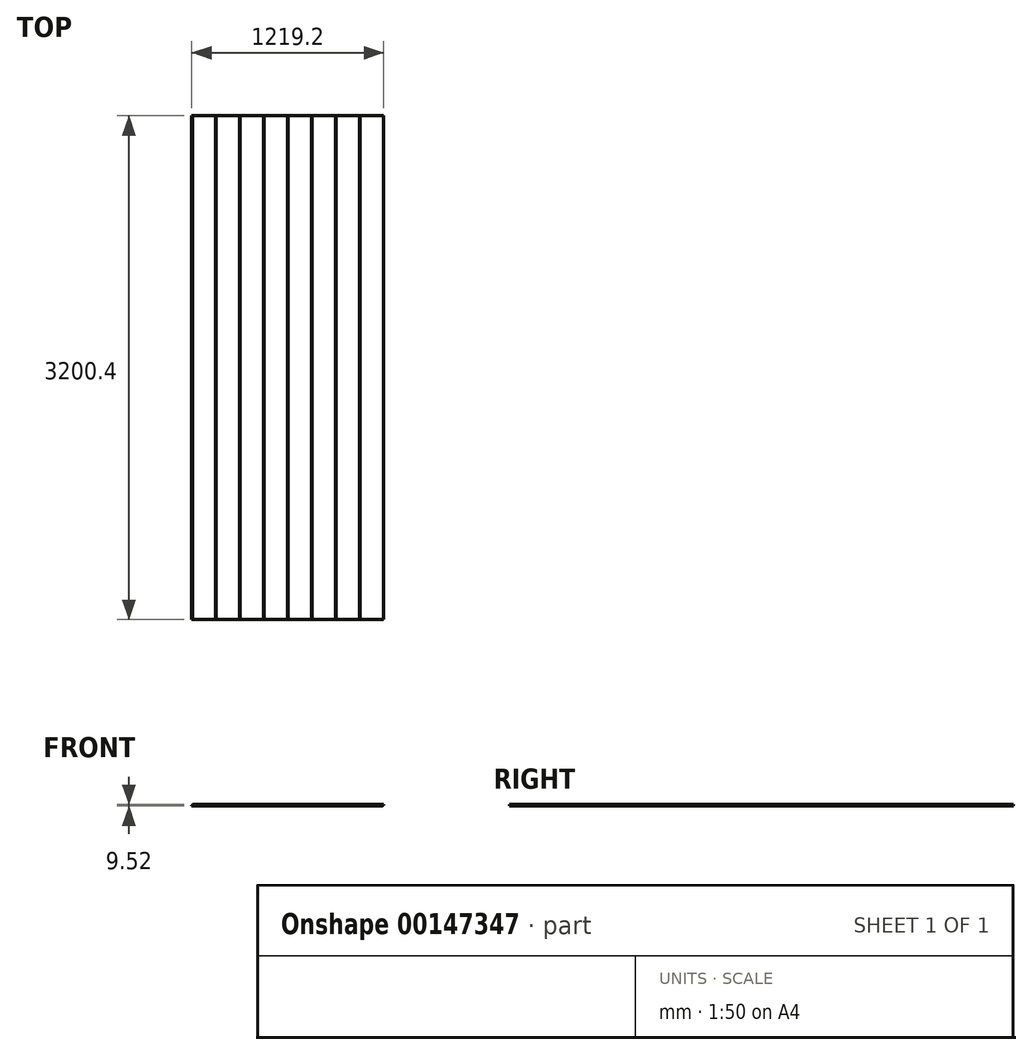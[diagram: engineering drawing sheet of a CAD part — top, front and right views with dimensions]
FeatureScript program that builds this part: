
annotation { "Feature Type Name" : "Feature", "Feature Type Description" : "" }
export const myFeature = defineFeature(function(context is Context, id is Id, definition is map)
    precondition{}
    {
        {
            var Q0;
            Q0=qCreatedBy(makeId("Top.planeOp"),FACE);
            var sketch = newSketch(context, id + "F0", { "sketchPlane" : qUnion([Q0])});
            skLineSegment(sketch, "E0.bottom", {"start": v(-609.6, 3130.65) * mm, "end": v(609.6, 3130.65) * mm});
            skLineSegment(sketch, "E0.top", {"start": v(-609.6, -523.78) * mm, "end": v(609.6, -523.78) * mm});
            skLineSegment(sketch, "E0.left", {"start": v(-609.6, 3130.65) * mm, "end": v(-609.6, -523.78) * mm});
            skLineSegment(sketch, "E0.right", {"start": v(609.6, 3130.65) * mm, "end": v(609.6, -523.78) * mm});
            skSolve(sketch);
        }
        {
            var Q0;
            Q0=qSketchRegion(id+"F0",true);
            extrude(context, id + "F1", {"entities" : qUnion([Q0]), "endBound" : BoundingType.SYMMETRIC, "depth" : 9.52 * mm});
        }
        {
            var Q0;
            Q0=makeQuery(id+"F1.opExtrude","SWEPT_FACE",FACE,{"disambiguationData":[OSD([sQuery(id+"F0.wireOp",EDGE,"E0.top")])]});
            var sketch = newSketch(context, id + "F2", { "sketchPlane" : qUnion([Q0])});
            skLineSegment(sketch, "E1", {"start": v(609.6, 0) * mm, "end": v(603.25, 0) * mm});
            skPoint(sketch, "E1.endSnap0", {"position": v(609.6, 0) * mm});
            skLineSegment(sketch, "E2", {"start": v(603.25, 0) * mm, "end": v(603.25, -4.76) * mm});
            skLineSegment(sketch, "E3", {"start": v(609.6, 0) * mm, "end": v(609.6, -4.76) * mm});
            skLineSegment(sketch, "E4", {"start": v(609.6, -4.76) * mm, "end": v(603.25, -4.76) * mm});
            skLineSegment(sketch, "E5.bottom", {"start": v(-609.6, 4.76) * mm, "end": v(-603.25, 4.76) * mm});
            skLineSegment(sketch, "E5.top", {"start": v(-609.6, 0) * mm, "end": v(-603.25, 0) * mm});
            skLineSegment(sketch, "E5.left", {"start": v(-609.6, 4.76) * mm, "end": v(-609.6, 0) * mm});
            skLineSegment(sketch, "E5.right", {"start": v(-603.25, 4.76) * mm, "end": v(-603.25, 0) * mm});
            skSolve(sketch);
        }
        {
            var Q0;
            Q0=qSketchRegion(id+"F2",true);
            extrude(context, id + "F3", {"entities" : qUnion([Q0]), "operationType" : NewBodyOperationType.REMOVE, "endBound" : BoundingType.THROUGH_ALL, "oppositeDirection" : true, "depth" : 25.4 * mm});
        }
        {
            var Q0;
            Q0=makeQuery(id+"F1.opExtrude","SWEPT_FACE",FACE,{"disambiguationData":[OSD([sQuery(id+"F0.wireOp",EDGE,"E0.top")])]});
            var sketch = newSketch(context, id + "F4", { "sketchPlane" : qUnion([Q0])});
            skLineSegment(sketch, "E6.bottom", {"start": v(-458, 4.76) * mm, "end": v(-456.4, 4.76) * mm});
            skLineSegment(sketch, "E6.top", {"start": v(-458, 3.17) * mm, "end": v(-456.4, 3.17) * mm});
            skLineSegment(sketch, "E6.left", {"start": v(-458, 4.76) * mm, "end": v(-458, 3.17) * mm});
            skLineSegment(sketch, "E6.right", {"start": v(-456.4, 4.76) * mm, "end": v(-456.4, 3.17) * mm});
            skPoint(sketch, "E7", {"position": v(-457.2, 3.17) * mm});
            skPoint(sketch, "E8.1.0.0", {"position": v(-304.8, 3.17) * mm});
            skLineSegment(sketch, "E8.1.0.1", {"start": v(-305.6, 4.76) * mm, "end": v(-304, 4.76) * mm});
            skLineSegment(sketch, "E8.1.0.2", {"start": v(-305.6, 3.17) * mm, "end": v(-304, 3.17) * mm});
            skLineSegment(sketch, "E8.1.0.3", {"start": v(-305.6, 4.76) * mm, "end": v(-305.6, 3.17) * mm});
            skLineSegment(sketch, "E8.1.0.4", {"start": v(-304, 4.76) * mm, "end": v(-304, 3.17) * mm});
            skPoint(sketch, "E8.2.0.0", {"position": v(-152.4, 3.17) * mm});
            skLineSegment(sketch, "E8.2.0.1", {"start": v(-153.2, 4.76) * mm, "end": v(-151.6, 4.76) * mm});
            skLineSegment(sketch, "E8.2.0.2", {"start": v(-153.2, 3.17) * mm, "end": v(-151.6, 3.17) * mm});
            skLineSegment(sketch, "E8.2.0.3", {"start": v(-153.2, 4.76) * mm, "end": v(-153.2, 3.17) * mm});
            skLineSegment(sketch, "E8.2.0.4", {"start": v(-151.6, 4.76) * mm, "end": v(-151.6, 3.17) * mm});
            skPoint(sketch, "E8.3.0.0", {"position": v(0, 3.17) * mm});
            skLineSegment(sketch, "E8.3.0.1", {"start": v(-0.8, 4.76) * mm, "end": v(0.8, 4.76) * mm});
            skLineSegment(sketch, "E8.3.0.2", {"start": v(-0.8, 3.17) * mm, "end": v(0.8, 3.17) * mm});
            skLineSegment(sketch, "E8.3.0.3", {"start": v(-0.8, 4.76) * mm, "end": v(-0.8, 3.17) * mm});
            skLineSegment(sketch, "E8.3.0.4", {"start": v(0.8, 4.76) * mm, "end": v(0.8, 3.17) * mm});
            skPoint(sketch, "E8.4.0.0", {"position": v(152.4, 3.17) * mm});
            skLineSegment(sketch, "E8.4.0.1", {"start": v(151.6, 4.76) * mm, "end": v(153.2, 4.76) * mm});
            skLineSegment(sketch, "E8.4.0.2", {"start": v(151.6, 3.17) * mm, "end": v(153.2, 3.17) * mm});
            skLineSegment(sketch, "E8.4.0.3", {"start": v(151.6, 4.76) * mm, "end": v(151.6, 3.17) * mm});
            skLineSegment(sketch, "E8.4.0.4", {"start": v(153.2, 4.76) * mm, "end": v(153.2, 3.17) * mm});
            skPoint(sketch, "E8.5.0.0", {"position": v(304.8, 3.17) * mm});
            skLineSegment(sketch, "E8.5.0.1", {"start": v(304, 4.76) * mm, "end": v(305.6, 4.76) * mm});
            skLineSegment(sketch, "E8.5.0.2", {"start": v(304, 3.17) * mm, "end": v(305.6, 3.17) * mm});
            skLineSegment(sketch, "E8.5.0.3", {"start": v(304, 4.76) * mm, "end": v(304, 3.17) * mm});
            skLineSegment(sketch, "E8.5.0.4", {"start": v(305.6, 4.76) * mm, "end": v(305.6, 3.17) * mm});
            skPoint(sketch, "E8.6.0.0", {"position": v(457.2, 3.17) * mm});
            skLineSegment(sketch, "E8.6.0.1", {"start": v(456.4, 4.76) * mm, "end": v(458, 4.76) * mm});
            skLineSegment(sketch, "E8.6.0.2", {"start": v(456.4, 3.17) * mm, "end": v(458, 3.17) * mm});
            skLineSegment(sketch, "E8.6.0.3", {"start": v(456.4, 4.76) * mm, "end": v(456.4, 3.17) * mm});
            skLineSegment(sketch, "E8.6.0.4", {"start": v(458, 4.76) * mm, "end": v(458, 3.17) * mm});
            skLineSegment(sketch, "E8.direction1", {"start": v(-457.2, 3.17) * mm, "end": v(-304.8, 3.17) * mm, "construction": true});
            skSolve(sketch);
        }
        {
            var Q0;
            Q0=qSketchRegion(id+"F4",true);
            extrude(context, id + "F5", {"entities" : qUnion([Q0]), "operationType" : NewBodyOperationType.REMOVE, "endBound" : BoundingType.THROUGH_ALL, "oppositeDirection" : true, "depth" : 25.4 * mm});
        }
        {
            var Q0;
            Q0=makeQuery(id+"F1.opExtrude","SWEPT_FACE",FACE,{"disambiguationData":[OSD([sQuery(id+"F0.wireOp",EDGE,"E0.left")])]});
            var sketch = newSketch(context, id + "F6", { "sketchPlane" : qUnion([Q0])});
            skPoint(sketch, "E9.0", {"position": v(-3130.65, -4.76) * mm});
            skPoint(sketch, "E10.0", {"position": v(-3130.65, 4.76) * mm});
            skLineSegment(sketch, "E11.bottom", {"start": v(-3130.65, -4.76) * mm, "end": v(-2676.62, -4.76) * mm});
            skLineSegment(sketch, "E11.top", {"start": v(-3130.65, 4.76) * mm, "end": v(-2676.62, 4.76) * mm});
            skLineSegment(sketch, "E11.left", {"start": v(-3130.65, -4.76) * mm, "end": v(-3130.65, 4.76) * mm});
            skLineSegment(sketch, "E11.right", {"start": v(-2676.62, -4.76) * mm, "end": v(-2676.62, 4.76) * mm});
            skSolve(sketch);
        }
        {
            var Q0;
            Q0=qSketchRegion(id+"F6",true);
            extrude(context, id + "F7", {"entities" : qUnion([Q0]), "operationType" : NewBodyOperationType.REMOVE, "endBound" : BoundingType.THROUGH_ALL, "oppositeDirection" : true, "depth" : 25.4 * mm});
        }
    });
